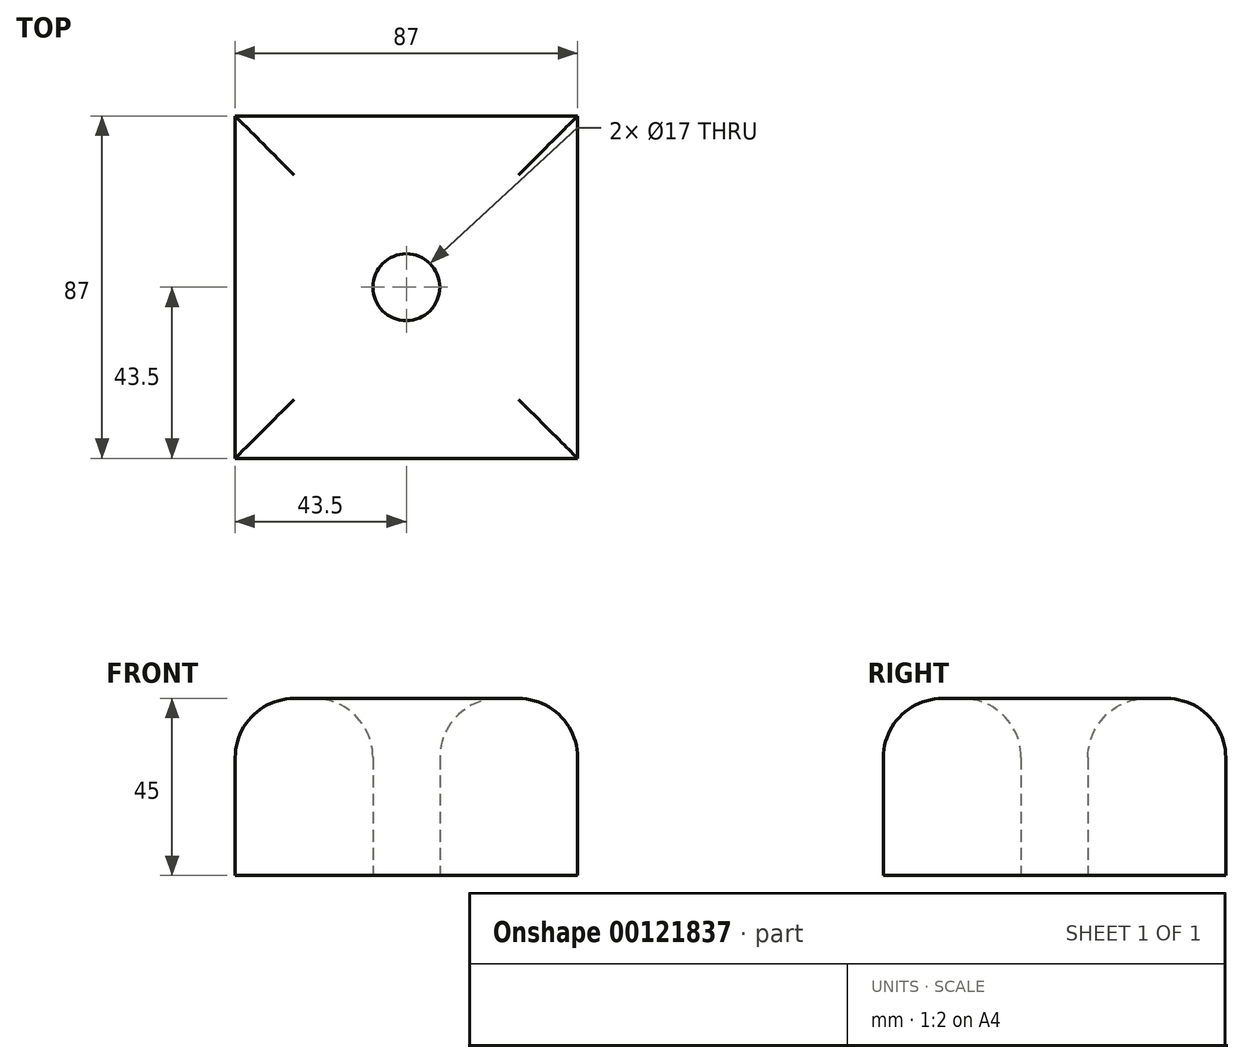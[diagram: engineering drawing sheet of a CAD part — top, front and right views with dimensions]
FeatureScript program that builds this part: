
annotation { "Feature Type Name" : "Feature", "Feature Type Description" : "" }
export const myFeature = defineFeature(function(context is Context, id is Id, definition is map)
    precondition{}
    {
        {
            var Q0;
            Q0=qCreatedBy(makeId("Top.planeOp"),FACE);
            var sketch = newSketch(context, id + "F0", { "sketchPlane" : qUnion([Q0])});
            skLineSegment(sketch, "E0.bottom", {"start": v(43.5, -43.5) * mm, "end": v(-43.5, -43.5) * mm});
            skLineSegment(sketch, "E0.top", {"start": v(43.5, 43.5) * mm, "end": v(-43.5, 43.5) * mm});
            skLineSegment(sketch, "E0.left", {"start": v(43.5, -43.5) * mm, "end": v(43.5, 43.5) * mm});
            skLineSegment(sketch, "E0.right", {"start": v(-43.5, -43.5) * mm, "end": v(-43.5, 43.5) * mm});
            skPoint(sketch, "E0.middle", {"position": v(0, 0) * mm});
            skCircle(sketch, "E1", {"center": v(0, 0) * mm, "radius": 8.5 * mm});
            skSolve(sketch);
        }
        {
            var Q0;
            Q0=makeQuery(id+"F0.imprint","IMPRINT",FACE,{"disambiguationData":[TD([[makeQuery(id+"F0.imprint","IMPRINT",EDGE,{"derivedFrom":sQuery(id+"F0.wireOp",EDGE,"E0.bottom")}),-1.0]])]});
            extrude(context, id + "F1", {"entities" : qUnion([Q0]), "depth" : 45 * mm});
        }
        {
            var Q0;
            Q0=makeQuery(id+"F1.opExtrude","CAP_FACE",FACE,{"disambiguationData":[OSD([sQuery(id+"F0.wireOp",EDGE,"E0.bottom"),sQuery(id+"F0.wireOp",EDGE,"E0.top"),sQuery(id+"F0.wireOp",EDGE,"E0.left"),sQuery(id+"F0.wireOp",EDGE,"E0.right"),sQuery(id+"F0.wireOp",EDGE,"E1")])],"isStart":false});
            fillet(context, id + "F2", {"entities" : qUnion([Q0]), "radius" : 15 * mm, "allowEdgeOverflow" : false});
        }
    });
